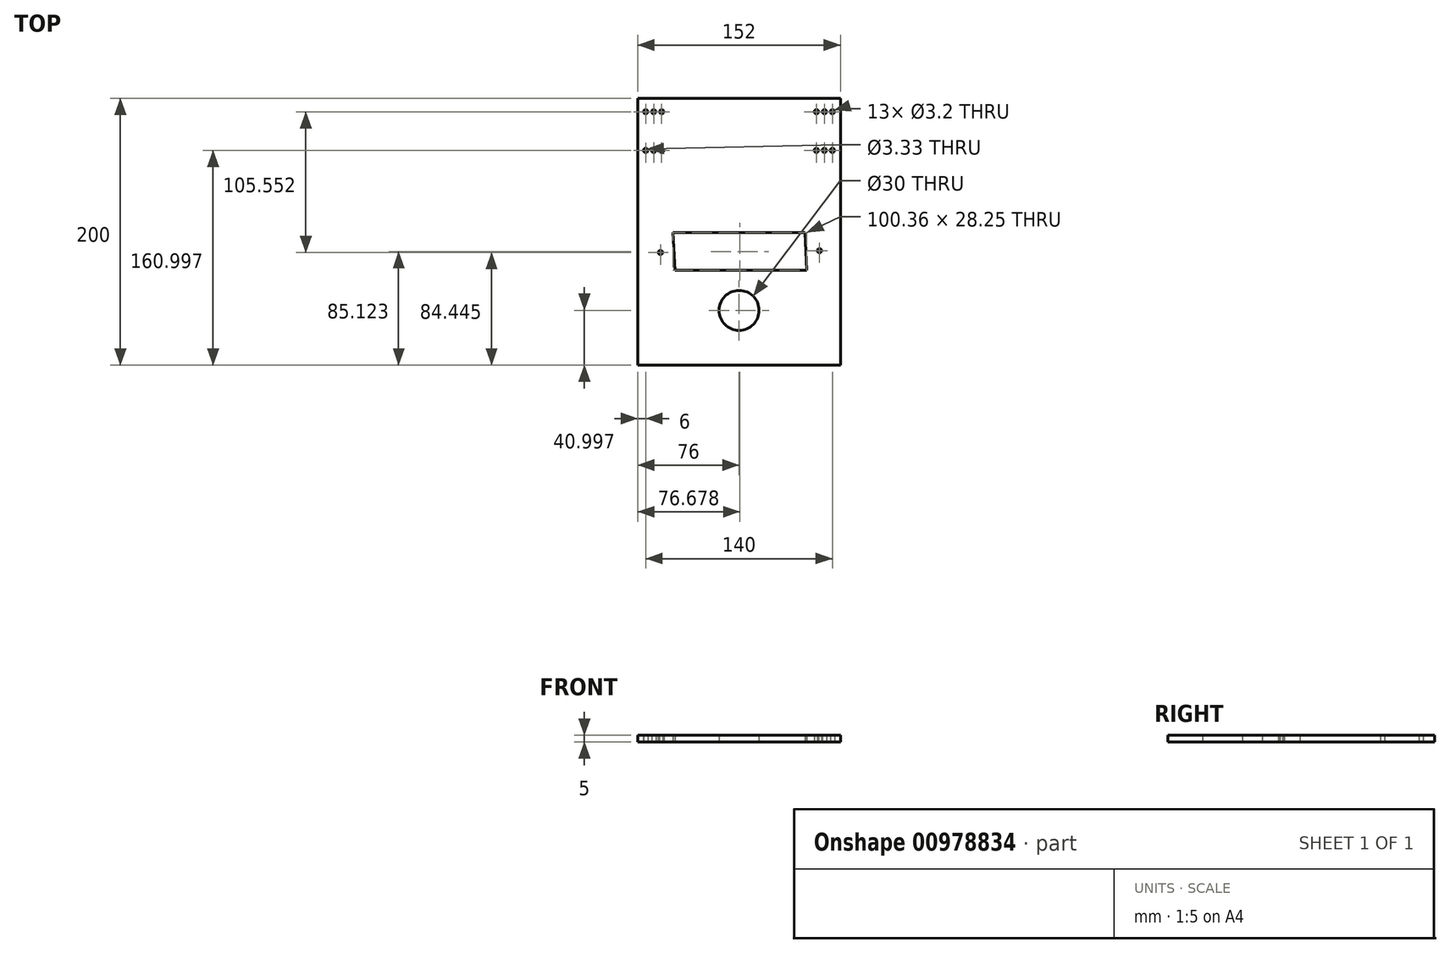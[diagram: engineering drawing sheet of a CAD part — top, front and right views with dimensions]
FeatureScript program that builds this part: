
annotation { "Feature Type Name" : "Feature", "Feature Type Description" : "" }
export const myFeature = defineFeature(function(context is Context, id is Id, definition is map)
    precondition{}
    {
        {
            var Q0;
            Q0=qCreatedBy(makeId("Top.planeOp"),FACE);
            var sketch = newSketch(context, id + "F0", { "sketchPlane" : qUnion([Q0])});
            skLineSegment(sketch, "E0.bottom", {"start": v(-76, 88.03) * mm, "end": v(76, 88.03) * mm});
            skLineSegment(sketch, "E0.top", {"start": v(-76, -111.97) * mm, "end": v(76, -111.97) * mm});
            skLineSegment(sketch, "E0.left", {"start": v(-76, 88.03) * mm, "end": v(-76, -111.97) * mm});
            skLineSegment(sketch, "E0.right", {"start": v(76, 88.03) * mm, "end": v(76, -111.97) * mm});
            skCircle(sketch, "E1", {"center": v(-70, 78.03) * mm, "radius": 1.6 * mm});
            skCircle(sketch, "E2.1.0.0", {"center": v(-64, 78.03) * mm, "radius": 1.6 * mm});
            skCircle(sketch, "E2.1.1.0", {"center": v(-64, 49.03) * mm, "radius": 1.6 * mm});
            skCircle(sketch, "E2.2.0.0", {"center": v(-58, 78.03) * mm, "radius": 1.6 * mm});
            skCircle(sketch, "E2.2.1.0", {"center": v(-58, 49.03) * mm, "radius": 1.6 * mm});
            skLineSegment(sketch, "E2.direction1", {"start": v(-70, 78.03) * mm, "end": v(-64, 78.03) * mm, "construction": true});
            skLineSegment(sketch, "E3.bottom", {"start": v(-49.5, -12.72) * mm, "end": v(49.5, -12.72) * mm});
            skLineSegment(sketch, "E3.top", {"start": v(-48.14, -40.97) * mm, "end": v(50.86, -40.97) * mm});
            skCircle(sketch, "E4", {"center": v(0, -70.97) * mm, "radius": 15 * mm});
            skLineSegment(sketch, "E5", {"start": v(-49.5, -12.72) * mm, "end": v(-62.95, -27.52) * mm});
            skLineSegment(sketch, "E6", {"start": v(-62.95, -27.52) * mm, "end": v(-48.14, -40.97) * mm});
            skLineSegment(sketch, "E7", {"start": v(50.86, -40.97) * mm, "end": v(64.3, -26.17) * mm});
            skLineSegment(sketch, "E8", {"start": v(49.5, -12.72) * mm, "end": v(64.3, -26.17) * mm});
            skLineSegment(sketch, "E9", {"start": v(0, 88.03) * mm, "end": v(0, 28.77) * mm});
            skCircle(sketch, "E10.MirrorC", {"center": v(58, 49.03) * mm, "radius": 1.6 * mm});
            skCircle(sketch, "E11.MirrorC", {"center": v(64, 49.03) * mm, "radius": 1.6 * mm});
            skCircle(sketch, "E12.MirrorC", {"center": v(70, 49.03) * mm, "radius": 1.6 * mm});
            skCircle(sketch, "E13.MirrorC", {"center": v(58, 78.03) * mm, "radius": 1.6 * mm});
            skCircle(sketch, "E14.MirrorC", {"center": v(64, 78.03) * mm, "radius": 1.6 * mm});
            skCircle(sketch, "E15.MirrorC", {"center": v(70, 78.03) * mm, "radius": 1.6 * mm});
            skCircle(sketch, "E16", {"center": v(-70, 49.03) * mm, "radius": 1.67 * mm});
            skCircle(sketch, "E17", {"center": v(60.3, -26.17) * mm, "radius": 1.6 * mm});
            skCircle(sketch, "E18", {"center": v(-58.95, -27.52) * mm, "radius": 1.6 * mm});
            skLineSegment(sketch, "E19", {"start": v(-49.5, -12.72) * mm, "end": v(-48.14, -40.97) * mm});
            skLineSegment(sketch, "E20", {"start": v(49.5, -12.72) * mm, "end": v(50.86, -40.97) * mm});
            skPoint(sketch, "E21.end.orphan", {"position": v(-153.39, -40.04) * mm});
            skPoint(sketch, "E21.start.orphan", {"position": v(-153.39, 43.11) * mm});
            skPoint(sketch, "E22.start.orphan", {"position": v(137.65, 43.11) * mm});
            skPoint(sketch, "E23.start.orphan", {"position": v(137.65, -40.04) * mm});
            skSolve(sketch);
        }
        {
            var Q0;
            Q0 = qSketchRegion(id + "F0", true);
            extrude(context, id + "F1", {"entities" : qUnion([Q0]), "depth" : 5 * mm, "offsetDistance" : 25 * mm});
        }
        {
            var Q0;
            Q0=makeQuery(id+"F0.imprint","IMPRINT",FACE,{"disambiguationData":[TD([[makeQuery(id+"F0.imprint","IMPRINT",EDGE,{"derivedFrom":sQuery(id+"F0.wireOp",EDGE,"E5")}),1.0]])]});
            var Q1;
            Q1=makeQuery(id+"F0.imprint","IMPRINT",FACE,{"disambiguationData":[TD([[makeQuery(id+"F0.imprint","IMPRINT",EDGE,{"derivedFrom":sQuery(id+"F0.wireOp",EDGE,"E7")}),1.0]])]});
            extrude(context, id + "F2", {"entities" : qUnion([Q0, Q1]), "operationType" : NewBodyOperationType.ADD, "depth" : 5 * mm, "offsetDistance" : 25 * mm});
        }
    });
